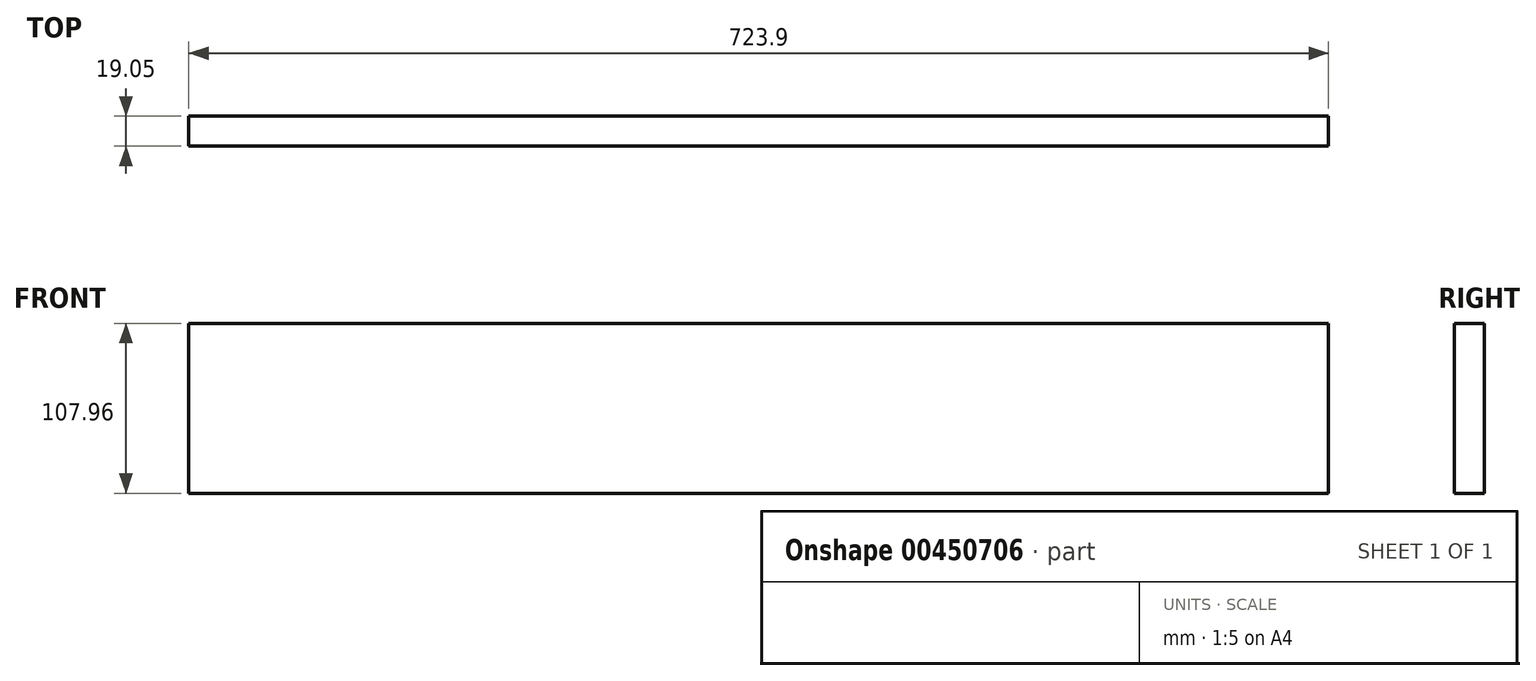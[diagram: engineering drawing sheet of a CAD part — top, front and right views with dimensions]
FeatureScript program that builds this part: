
annotation { "Feature Type Name" : "Feature", "Feature Type Description" : "" }
export const myFeature = defineFeature(function(context is Context, id is Id, definition is map)
    precondition{}
    {
        {
            var Q0;
            Q0=qCreatedBy(makeId("Front.planeOp"),FACE);
            var sketch = newSketch(context, id + "F0", { "sketchPlane" : qUnion([Q0])});
            skLineSegment(sketch, "E0.bottom", {"start": v(-361.95, 53.97) * mm, "end": v(361.95, 53.97) * mm});
            skLineSegment(sketch, "E0.top", {"start": v(-361.95, -53.97) * mm, "end": v(361.95, -53.97) * mm});
            skLineSegment(sketch, "E0.left", {"start": v(-361.95, 53.97) * mm, "end": v(-361.95, -53.97) * mm});
            skLineSegment(sketch, "E0.right", {"start": v(361.95, 53.97) * mm, "end": v(361.95, -53.97) * mm});
            skPoint(sketch, "E0.middle", {"position": v(0, 0) * mm});
            skSolve(sketch);
        }
        {
            var Q0;
            Q0=makeQuery(id+"F0.imprint","IMPRINT",FACE,{"disambiguationData":[TD([[makeQuery(id+"F0.imprint","IMPRINT",EDGE,{"derivedFrom":sQuery(id+"F0.wireOp",EDGE,"E0.bottom")}),-1.0]])]});
            extrude(context, id + "F1", {"entities" : qUnion([Q0]), "depth" : 19.05 * mm});
        }
    });
